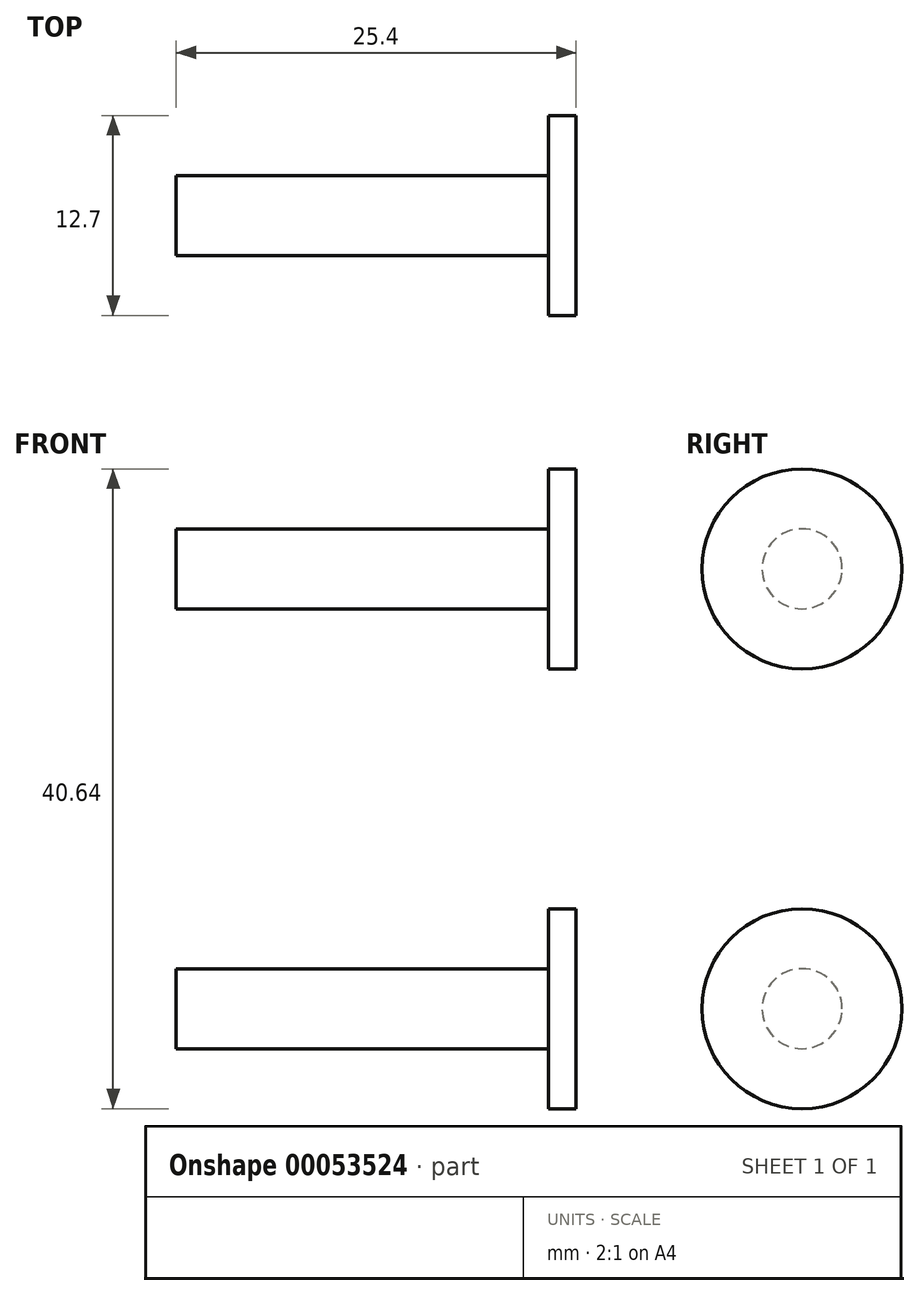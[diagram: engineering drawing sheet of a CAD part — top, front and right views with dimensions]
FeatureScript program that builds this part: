
annotation { "Feature Type Name" : "Feature", "Feature Type Description" : "" }
export const myFeature = defineFeature(function(context is Context, id is Id, definition is map)
    precondition{}
    {
        {
            var Q0;
            Q0=qCreatedBy(makeId("Front.planeOp"),FACE);
            var sketch = newSketch(context, id + "F0", { "sketchPlane" : qUnion([Q0])});
            skLineSegment(sketch, "E0.rect.bottom", {"start": v(12.7, -1.27) * mm, "end": v(-12.7, -1.27) * mm});
            skLineSegment(sketch, "E0.rect.top", {"start": v(12.7, 1.27) * mm, "end": v(-12.7, 1.27) * mm});
            skLineSegment(sketch, "E0.rect.left", {"start": v(12.7, -1.27) * mm, "end": v(12.7, 1.27) * mm});
            skLineSegment(sketch, "E0.rect.right", {"start": v(-12.7, -1.27) * mm, "end": v(-12.7, 1.27) * mm});
            skPoint(sketch, "E0.rect.middle", {"position": v(0, 0) * mm});
            skLineSegment(sketch, "E1.bottom", {"start": v(12.7, 1.27) * mm, "end": v(10.96, 1.27) * mm});
            skLineSegment(sketch, "E1.top", {"start": v(12.7, 5.08) * mm, "end": v(10.96, 5.08) * mm});
            skLineSegment(sketch, "E1.left", {"start": v(12.7, 1.27) * mm, "end": v(12.7, 5.08) * mm});
            skLineSegment(sketch, "E1.right", {"start": v(10.96, 1.27) * mm, "end": v(10.96, 5.08) * mm});
            skSolve(sketch);
        }
        {
            var Q0;
            Q0 = qSketchRegion(id + "F0", true);
            var Q1;
            Q1=sQuery(id+"F0.wireOp",EDGE,"E0.rect.bottom");
            revolve(context, id + "F1", {"entities" : qUnion([Q0]), "axis" : qUnion([Q1]), "revolveType" : RevolveType.FULL});
        }
        {
            var Q0;
            Q0=qCreatedBy(makeId("Top.planeOp"),FACE);
            cPlane(context, id + "F2", {"entities" : qUnion([Q0]), "cplaneType" : CPlaneType.OFFSET, "offset" : 12.7 * mm, "width" : 152.4 * mm, "height" : 152.4 * mm});
        }
        {
            var Q0;
            Q0=makeQuery(id+"F1.opRevolve","SWEPT_BODY",BODY,{"disambiguationData":[OSD([sQuery(id+"F0.wireOp",EDGE,"E0.rect.bottom"),sQuery(id+"F0.wireOp",EDGE,"E0.rect.top"),sQuery(id+"F0.wireOp",EDGE,"E0.rect.left"),sQuery(id+"F0.wireOp",EDGE,"E0.rect.right"),sQuery(id+"F0.wireOp",EDGE,"E1.top"),sQuery(id+"F0.wireOp",EDGE,"E1.left"),sQuery(id+"F0.wireOp",EDGE,"E1.right")])]});
            var Q1;
            Q1=qCreatedBy(id+"F2.planeOp",FACE);
            mirror(context, id + "F3", {"entities" : qUnion([Q0]), "mirrorPlane" : qUnion([Q1])});
        }
    });
